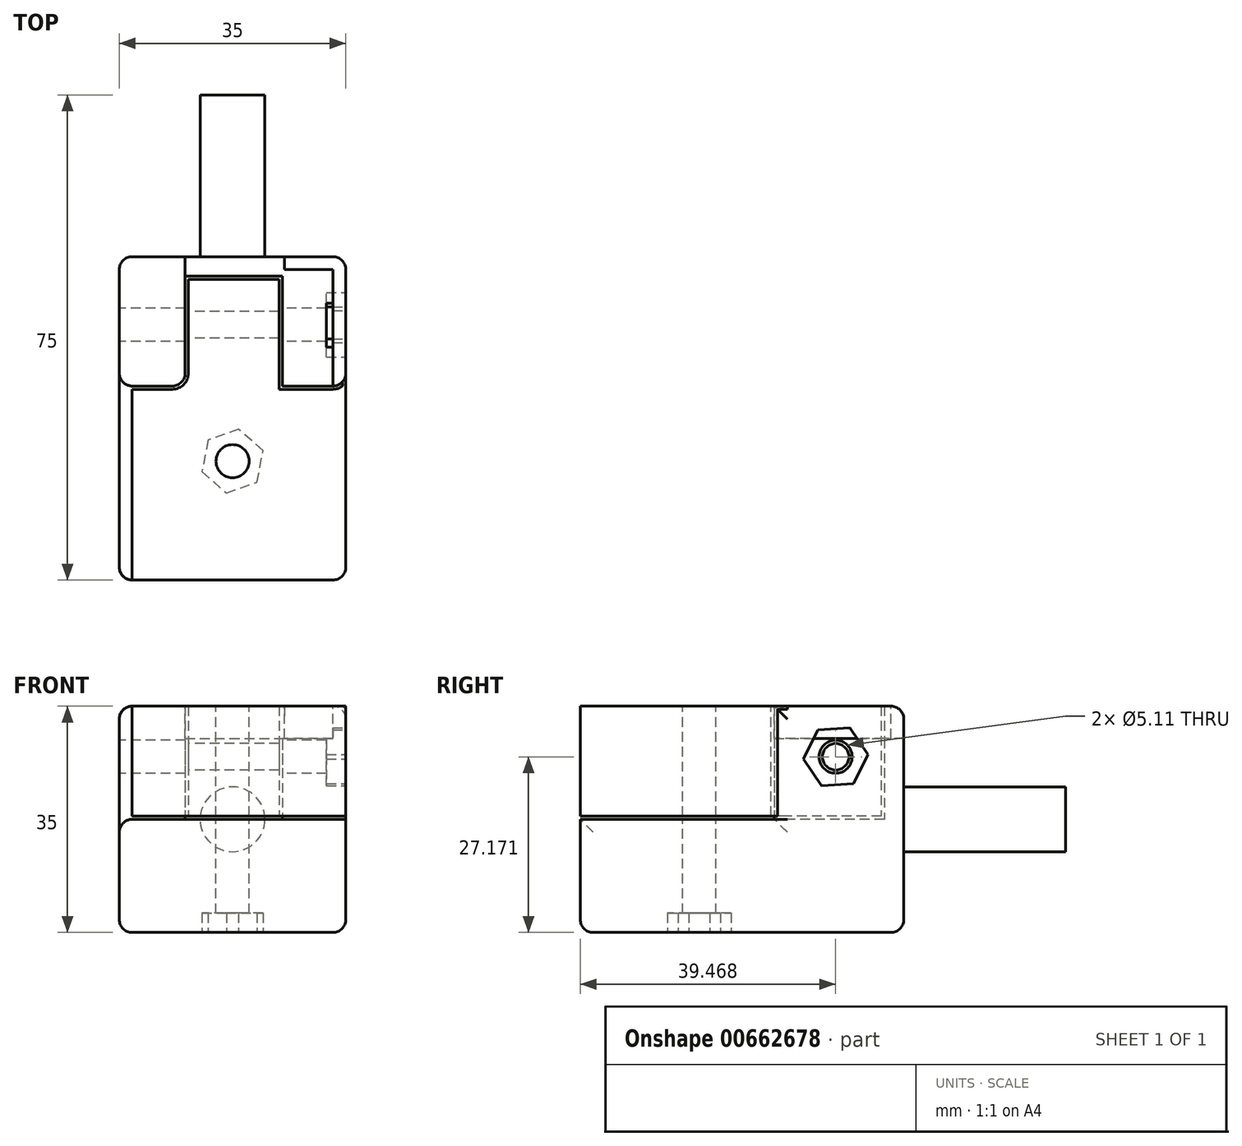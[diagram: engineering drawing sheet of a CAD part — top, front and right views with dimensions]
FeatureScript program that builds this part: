
annotation { "Feature Type Name" : "Feature", "Feature Type Description" : "" }
export const myFeature = defineFeature(function(context is Context, id is Id, definition is map)
    precondition{}
    {
        {
            var Q0;
            Q0=qCreatedBy(makeId("Front.planeOp"),FACE);
            var sketch = newSketch(context, id + "F0", { "sketchPlane" : qUnion([Q0])});
            skLineSegment(sketch, "E0.bottom", {"start": v(-17.5, -17.5) * mm, "end": v(17.5, -17.5) * mm});
            skLineSegment(sketch, "E0.top", {"start": v(-17.5, 17.5) * mm, "end": v(17.5, 17.5) * mm});
            skLineSegment(sketch, "E0.left", {"start": v(-17.5, -17.5) * mm, "end": v(-17.5, 17.5) * mm});
            skLineSegment(sketch, "E0.right", {"start": v(17.5, -17.5) * mm, "end": v(17.5, 17.5) * mm});
            skPoint(sketch, "E0.middle", {"position": v(0, 0) * mm});
            skSolve(sketch);
        }
        {
            var Q0;
            Q0=makeQuery(id+"F0.imprint","IMPRINT",FACE,{"disambiguationData":[TD([[makeQuery(id+"F0.imprint","IMPRINT",EDGE,{"derivedFrom":sQuery(id+"F0.wireOp",EDGE,"E0.bottom")}),1.0]])]});
            var Q1;
            Q1 = qSketchRegion(id + "F0", true);
            extrude(context, id + "F1", {"entities" : qUnion([Q0, Q1]), "depth" : 50 * mm, "offsetDistance" : 25 * mm});
        }
        {
            var Q0;
            Q0=makeQuery(id+"F1.opExtrude","SWEPT_FACE",FACE,{"disambiguationData":[OSD([sQuery(id+"F0.wireOp",EDGE,"E0.left")])]});
            var sketch = newSketch(context, id + "F2", { "sketchPlane" : qUnion([Q0])});
            skLineSegment(sketch, "E1.bottom", {"start": v(20, 17.5) * mm, "end": v(50, 17.5) * mm});
            skLineSegment(sketch, "E1.top", {"start": v(20, 0) * mm, "end": v(50, 0) * mm});
            skLineSegment(sketch, "E1.left", {"start": v(20, 17.5) * mm, "end": v(20, 0) * mm});
            skLineSegment(sketch, "E1.right", {"start": v(50, 17.5) * mm, "end": v(50, 0) * mm});
            skSolve(sketch);
        }
        {
            var Q0;
            Q0=makeQuery(id+"F2.imprint","IMPRINT",FACE,{"disambiguationData":[TD([[makeQuery(id+"F2.imprint","IMPRINT",EDGE,{"derivedFrom":sQuery(id+"F2.wireOp",EDGE,"E1.bottom")}),1.0]])]});
            extrude(context, id + "F3", {"entities" : qUnion([Q0]), "operationType" : NewBodyOperationType.REMOVE, "endBound" : BoundingType.THROUGH_ALL, "oppositeDirection" : true, "depth" : 25 * mm, "offsetDistance" : 25 * mm});
        }
        {
            var Q0;
            Q0=makeQuery(id+"F3.boolean.opBoolean","COPY",FACE,{"derivedFrom":makeQuery(id+"F3.opExtrude","SWEPT_FACE",FACE,{"disambiguationData":[OSD([sQuery(id+"F2.wireOp",EDGE,"E1.left")])]})});
            var sketch = newSketch(context, id + "F4", { "sketchPlane" : qUnion([Q0])});
            skLineSegment(sketch, "E2.bottom", {"start": v(-7.31, 17.5) * mm, "end": v(7.69, 17.5) * mm});
            skLineSegment(sketch, "E2.top", {"start": v(-7.31, 0) * mm, "end": v(7.69, 0) * mm});
            skLineSegment(sketch, "E2.left", {"start": v(-7.31, 17.5) * mm, "end": v(-7.31, 0) * mm});
            skLineSegment(sketch, "E2.right", {"start": v(7.69, 17.5) * mm, "end": v(7.69, 0) * mm});
            skSolve(sketch);
        }
        {
            var Q0;
            Q0=makeQuery(id+"F4.imprint","IMPRINT",FACE,{"disambiguationData":[TD([[makeQuery(id+"F4.imprint","IMPRINT",EDGE,{"derivedFrom":sQuery(id+"F4.wireOp",EDGE,"E2.bottom")}),1.0]])]});
            extrude(context, id + "F5", {"entities" : qUnion([Q0]), "operationType" : NewBodyOperationType.REMOVE, "oppositeDirection" : true, "depth" : 17 * mm, "offsetDistance" : 25 * mm});
        }
        {
            var Q0;
            Q0=makeQuery(id+"F1.opExtrude","SWEPT_EDGE",EDGE,{"disambiguationData":[OSD([sQuery(id+"F0.wireOp",EDGE,"E0.top"),sQuery(id+"F0.wireOp",EDGE,"E0.left")])]});
            var Q1;
            Q1=makeQuery(id+"F1.opExtrude","SWEPT_FACE",FACE,{"disambiguationData":[OSD([sQuery(id+"F0.wireOp",EDGE,"E0.left")])]});
            var Q2;
            Q2=makeQuery(id+"F1.opExtrude","CAP_EDGE",EDGE,{"disambiguationData":[OSD([sQuery(id+"F0.wireOp",EDGE,"E0.bottom")])],"isStart":false});
            var Q3;
            Q3=makeQuery(id+"F1.opExtrude","CAP_EDGE",EDGE,{"disambiguationData":[OSD([sQuery(id+"F0.wireOp",EDGE,"E0.right")])],"isStart":false});
            var Q4;
            Q4=makeQuery(id+"F1.opExtrude","SWEPT_EDGE",EDGE,{"disambiguationData":[OSD([sQuery(id+"F0.wireOp",EDGE,"E0.bottom"),sQuery(id+"F0.wireOp",EDGE,"E0.right")])]});
            var Q5;
            Q5=makeQuery(id+"F1.opExtrude","CAP_EDGE",EDGE,{"disambiguationData":[OSD([sQuery(id+"F0.wireOp",EDGE,"E0.right")])],"isStart":true});
            var Q6;
            Q6=makeQuery(id+"F1.opExtrude","SWEPT_EDGE",EDGE,{"disambiguationData":[OSD([sQuery(id+"F0.wireOp",EDGE,"E0.top"),sQuery(id+"F0.wireOp",EDGE,"E0.right")])]});
            var Q7;
            Q7=makeQuery(id+"F3.boolean.opBoolean","INTERSECT",EDGE,{"derivedFrom":[makeQuery(id+"F1.opExtrude","SWEPT_FACE",FACE,{"disambiguationData":[OSD([sQuery(id+"F0.wireOp",EDGE,"E0.right")])]}),makeQuery(id+"F3.opExtrude","SWEPT_FACE",FACE,{"disambiguationData":[OSD([sQuery(id+"F2.wireOp",EDGE,"E1.left")])]})]});
            var Q8;
            Q8=makeQuery(id+"F1.opExtrude","CAP_EDGE",EDGE,{"disambiguationData":[OSD([sQuery(id+"F0.wireOp",EDGE,"E0.top")])],"isStart":true});
            var Q9;
            Q9=makeQuery(id+"F1.opExtrude","CAP_EDGE",EDGE,{"disambiguationData":[OSD([sQuery(id+"F0.wireOp",EDGE,"E0.bottom")])],"isStart":true});
            var Q10;
            Q10=makeQuery(id+"F5.boolean.opBoolean","COPY",EDGE,{"derivedFrom":makeQuery(id+"F5.opExtrude","SWEPT_EDGE",EDGE,{"disambiguationData":[OSD([sQuery(id+"F0.wireOp",EDGE,"E0.top"),sQuery(id+"F0.wireOp",EDGE,"E0.left"),sQuery(id+"F2.wireOp",EDGE,"E1.bottom"),sQuery(id+"F2.wireOp",EDGE,"E1.left"),sQuery(id+"F4.wireOp",EDGE,"E2.bottom"),sQuery(id+"F4.wireOp",EDGE,"E2.left")])]})});
            var Q11;
            Q11=makeQuery(id+"F5.boolean.opBoolean","COPY",EDGE,{"derivedFrom":makeQuery(id+"F5.opExtrude","SWEPT_EDGE",EDGE,{"disambiguationData":[OSD([sQuery(id+"F0.wireOp",EDGE,"E0.top"),sQuery(id+"F0.wireOp",EDGE,"E0.left"),sQuery(id+"F2.wireOp",EDGE,"E1.bottom"),sQuery(id+"F2.wireOp",EDGE,"E1.left"),sQuery(id+"F4.wireOp",EDGE,"E2.bottom"),sQuery(id+"F4.wireOp",EDGE,"E2.right")])]})});
            var Q12;
            Q12=makeQuery(id+"F5.boolean.opBoolean","COPY",EDGE,{"derivedFrom":makeQuery(id+"F5.opExtrude","CAP_EDGE",EDGE,{"disambiguationData":[OSD([sQuery(id+"F4.wireOp",EDGE,"E2.left")])],"isStart":true})});
            var Q13;
            Q13=makeQuery(id+"F5.boolean.opBoolean","COPY",EDGE,{"derivedFrom":makeQuery(id+"F5.opExtrude","CAP_EDGE",EDGE,{"disambiguationData":[OSD([sQuery(id+"F4.wireOp",EDGE,"E2.right")])],"isStart":true})});
            var Q14;
            {var subQ0=sQuery(id+"F0.wireOp",EDGE,"E0.top");var subQ1=sQuery(id+"F0.wireOp",EDGE,"E0.left");var subQ2=sQuery(id+"F2.wireOp",EDGE,"E1.left");Q14=makeQuery(id+"F5.boolean.opBoolean","SPLIT",EDGE,{"disambiguationData":[TD([makeQuery(id+"F1.opExtrude","SWEPT_FACE",FACE,{"disambiguationData":[OSD([subQ1])]})])],"derivedFrom":makeQuery(id+"F3.boolean.opBoolean","COPY",EDGE,{"derivedFrom":makeQuery(id+"F3.opExtrude","SWEPT_EDGE",EDGE,{"disambiguationData":[OSD([subQ0,subQ1,sQuery(id+"F2.wireOp",EDGE,"E1.bottom"),subQ2])]})})});}
            var Q15;
            {var subQ0=sQuery(id+"F0.wireOp",EDGE,"E0.top");var subQ1=sQuery(id+"F2.wireOp",EDGE,"E1.left");Q15=makeQuery(id+"F5.boolean.opBoolean","SPLIT",EDGE,{"disambiguationData":[TD([makeQuery(id+"F1.opExtrude","SWEPT_FACE",FACE,{"disambiguationData":[OSD([sQuery(id+"F0.wireOp",EDGE,"E0.right")])]})])],"derivedFrom":makeQuery(id+"F3.boolean.opBoolean","COPY",EDGE,{"derivedFrom":makeQuery(id+"F3.opExtrude","SWEPT_EDGE",EDGE,{"disambiguationData":[OSD([subQ0,sQuery(id+"F0.wireOp",EDGE,"E0.left"),sQuery(id+"F2.wireOp",EDGE,"E1.bottom"),subQ1])]})})});}
            fillet(context, id + "F6", {"entities" : qUnion([Q0, Q1, Q2, Q3, Q4, Q5, Q6, Q7, Q8, Q9, Q10, Q11, Q12, Q13, Q14, Q15]), "radius" : 2 * mm, "tangentPropagation" : true, "allowEdgeOverflow" : false});
        }
        {
            var Q0;
            Q0=makeQuery(id+"F1.opExtrude","CAP_FACE",FACE,{"disambiguationData":[OSD([sQuery(id+"F0.wireOp",EDGE,"E0.bottom"),sQuery(id+"F0.wireOp",EDGE,"E0.top"),sQuery(id+"F0.wireOp",EDGE,"E0.left"),sQuery(id+"F0.wireOp",EDGE,"E0.right")])],"isStart":true});
            var sketch = newSketch(context, id + "F7", { "sketchPlane" : qUnion([Q0])});
            skCircle(sketch, "E3", {"center": v(0, 0) * mm, "radius": 5 * mm});
            skSolve(sketch);
        }
        {
            var Q0;
            Q0=makeQuery(id+"F7.imprint","IMPRINT",FACE,{"disambiguationData":[TD([[makeQuery(id+"F7.imprint","IMPRINT",EDGE,{"derivedFrom":sQuery(id+"F7.wireOp",EDGE,"E3")}),1.0]])]});
            extrude(context, id + "F8", {"entities" : qUnion([Q0]), "operationType" : NewBodyOperationType.ADD, "depth" : 25 * mm, "offsetDistance" : 25 * mm});
        }
        {
            var Q0;
            Q0=makeQuery(id+"F1.opExtrude","SWEPT_FACE",FACE,{"disambiguationData":[OSD([sQuery(id+"F0.wireOp",EDGE,"E0.left")])]});
            var sketch = newSketch(context, id + "F9", { "sketchPlane" : qUnion([Q0])});
            skPoint(sketch, "E4", {"position": v(10.53, 9.67) * mm});
            skSolve(sketch);
        }
        {
            var Q0;
            Q0=sQuery(id+"F9.wireOp",VERTEX,"E4");
            var Q1;
            Q1=makeQuery(id+"F1.opExtrude","SWEPT_BODY",BODY,{"disambiguationData":[OSD([sQuery(id+"F0.wireOp",EDGE,"E0.bottom"),sQuery(id+"F0.wireOp",EDGE,"E0.top"),sQuery(id+"F0.wireOp",EDGE,"E0.left"),sQuery(id+"F0.wireOp",EDGE,"E0.right")])]});
            hole(context, id + "F10", {"style" : HoleStyle.SIMPLE, "endStyle" : HoleEndStyle.BLIND, "standardTappedOrClearance" : lookupTablePath({ "standard" : "ANSI", "fit" : "Normal (ASME)", "size" : "#10", "type" : "Clearance" }), "standardBlindInLast" : lookupTablePath({ "fit" : "Free", "standard" : "ANSI", "size" : "#10", "type" : "Clearance" }), "holeDiameter" : 5.1 * mm, "majorDiameter" : 5 * mm, "holeDepth" : 60 * mm, "isTappedThrough" : true, "tappedDepth" : 12.7 * mm, "tapClearance" : 3, "locations" : qUnion([Q0]), "scope" : qUnion([Q1])});
        }
        {
            var Q0;
            Q0=makeQuery(id+"F5.boolean.opBoolean","MERGE",FACE,{"derivedFrom":[makeQuery(id+"F3.boolean.opBoolean","COPY",FACE,{"derivedFrom":makeQuery(id+"F3.opExtrude","SWEPT_FACE",FACE,{"disambiguationData":[OSD([sQuery(id+"F2.wireOp",EDGE,"E1.top")])]})}),makeQuery(id+"F5.opExtrude","SWEPT_FACE",FACE,{"disambiguationData":[OSD([sQuery(id+"F4.wireOp",EDGE,"E2.top")])]})]});
            var sketch = newSketch(context, id + "F11", { "sketchPlane" : qUnion([Q0])});
            skLineSegment(sketch, "E5.0", {"start": v(15.5, -50) * mm, "end": v(-15.5, -50) * mm});
            skLineSegment(sketch, "E6.0.0", {"start": v(-9.31, -20) * mm, "end": v(-15.5, -20) * mm});
            skLineSegment(sketch, "E6.0.1", {"start": v(-15.5, -20) * mm, "end": v(-15.5, -50) * mm});
            skLineSegment(sketch, "E6.0.2", {"start": v(-15.5, -50) * mm, "end": v(15.5, -50) * mm});
            skArc(sketch, "E6.0.3", {"start": v(15.5, -50) * mm, "mid": v(16.91, -49.41) * mm, "end": v(17.5, -48) * mm});
            skLineSegment(sketch, "E6.0.4", {"start": v(17.5, -48) * mm, "end": v(17.5, -18) * mm});
            skArc(sketch, "E6.0.5", {"start": v(17.5, -18) * mm, "mid": v(16.91, -19.41) * mm, "end": v(15.5, -20) * mm});
            skLineSegment(sketch, "E6.0.6", {"start": v(15.5, -20) * mm, "end": v(9.69, -20) * mm});
            skArc(sketch, "E6.0.7", {"start": v(9.69, -20) * mm, "mid": v(8.27, -19.41) * mm, "end": v(7.69, -18) * mm});
            skLineSegment(sketch, "E6.0.8", {"start": v(7.69, -18) * mm, "end": v(7.69, -3) * mm});
            skLineSegment(sketch, "E6.0.9", {"start": v(7.69, -3) * mm, "end": v(-7.31, -3) * mm});
            skLineSegment(sketch, "E6.0.10", {"start": v(-7.31, -3) * mm, "end": v(-7.31, -18) * mm});
            skArc(sketch, "E6.0.11", {"start": v(-7.31, -18) * mm, "mid": v(-7.9, -19.41) * mm, "end": v(-9.31, -20) * mm});
            skSolve(sketch);
        }
        {
            var Q0;
            Q0 = qSketchRegion(id + "F11", true);
            var Q1;
            Q1=makeQuery(id+"F1.opExtrude","SWEPT_FACE",FACE,{"disambiguationData":[OSD([sQuery(id+"F0.wireOp",EDGE,"E0.top")])]});
            extrude(context, id + "F12", {"entities" : qUnion([Q0]), "endBound" : BoundingType.UP_TO_SURFACE, "depth" : 25 * mm, "endBoundEntityFace" : qUnion([Q1]), "offsetDistance" : 25 * mm});
        }
        {
            var Q0;
            Q0=makeQuery(id+"F1.opExtrude","SWEPT_BODY",BODY,{"disambiguationData":[OSD([sQuery(id+"F0.wireOp",EDGE,"E0.bottom"),sQuery(id+"F0.wireOp",EDGE,"E0.top"),sQuery(id+"F0.wireOp",EDGE,"E0.left"),sQuery(id+"F0.wireOp",EDGE,"E0.right")])]});
            var Q1;
            Q1=makeQuery(id+"F12.opExtrude","SWEPT_BODY",BODY,{"disambiguationData":[OSD([sQuery(id+"F11.wireOp",EDGE,"E6.0.0"),sQuery(id+"F11.wireOp",EDGE,"E6.0.1"),sQuery(id+"F11.wireOp",EDGE,"E6.0.2"),sQuery(id+"F11.wireOp",EDGE,"E6.0.3"),sQuery(id+"F11.wireOp",EDGE,"E6.0.4"),sQuery(id+"F11.wireOp",EDGE,"E6.0.5"),sQuery(id+"F11.wireOp",EDGE,"E6.0.6"),sQuery(id+"F11.wireOp",EDGE,"E6.0.7"),sQuery(id+"F11.wireOp",EDGE,"E6.0.8"),sQuery(id+"F11.wireOp",EDGE,"E6.0.9"),sQuery(id+"F11.wireOp",EDGE,"E6.0.10"),sQuery(id+"F11.wireOp",EDGE,"E6.0.11")])]});
            booleanBodies(context, id + "F13", {"operationType" : BooleanOperationType.SUBTRACTION, "tools" : qUnion([Q0]), "targets" : qUnion([Q1]), "offset" : true, "offsetAll" : true, "offsetDistance" : .5 * mm, "keepTools" : true});
        }
        {
            var Q0;
            Q0=makeQuery(id+"F13.tempBoolean.opBoolean","SPLIT",FACE,{"disambiguationData":[TD([makeQuery(id+"F13.offsetTempBody.opPattern","COPY",FACE,{"derivedFrom":makeQuery(id+"F10.hole-0.boolean.opBoolean","COPY",FACE,{"disambiguationData":[TD([makeQuery(id+"F1.opExtrude","SWEPT_FACE",FACE,{"disambiguationData":[OSD([sQuery(id+"F0.wireOp",EDGE,"E0.left")])]})])],"derivedFrom":makeQuery(id+"F10.hole-0.opRevolve","SWEPT_FACE",FACE,{"disambiguationData":[OSD([sQuery(id+"F10.hole-0.sketch.wireOp",EDGE,"core_line_2")])]})}),"instanceName":"1"})])],"derivedFrom":makeQuery(id+"F12.opExtrude","SWEPT_FACE",FACE,{"disambiguationData":[OSD([sQuery(id+"F11.wireOp",EDGE,"E6.0.10")])]})});
            extrude(context, id + "F14", {"entities" : qUnion([Q0]), "operationType" : NewBodyOperationType.REMOVE, "endBound" : BoundingType.THROUGH_ALL, "oppositeDirection" : true, "depth" : 25 * mm, "offsetDistance" : 25 * mm});
        }
        {
            var Q0;
            Q0=makeQuery(id+"F1.opExtrude","SWEPT_FACE",FACE,{"disambiguationData":[OSD([sQuery(id+"F0.wireOp",EDGE,"E0.top")])]});
            var sketch = newSketch(context, id + "F15", { "sketchPlane" : qUnion([Q0])});
            skLineSegment(sketch, "E7.bottom", {"start": v(-7.36, 0) * mm, "end": v(8.03, 0) * mm});
            skLineSegment(sketch, "E7.top", {"start": v(-7.36, -3) * mm, "end": v(8.03, -3) * mm});
            skLineSegment(sketch, "E7.left", {"start": v(-7.36, 0) * mm, "end": v(-7.36, -3) * mm});
            skLineSegment(sketch, "E7.right", {"start": v(8.03, 0) * mm, "end": v(8.03, -3) * mm});
            skSolve(sketch);
        }
        {
            var Q0;
            {var subQ0=sQuery(id+"F15.wireOp",EDGE,"E7.bottom");Q0=makeQuery(id+"F15.imprint","IMPRINT",FACE,{"disambiguationData":[TD([[makeQuery(id+"F15.imprint","IMPRINT",EDGE,{"derivedFrom":subQ0}),-1.0]])]});}
            var Q1;
            {var subQ0=sQuery(id+"F15.wireOp",EDGE,"E7.top");Q1=makeQuery(id+"F15.imprint","IMPRINT",FACE,{"disambiguationData":[TD([[makeQuery(id+"F15.imprint","IMPRINT",EDGE,{"derivedFrom":subQ0}),-1.0]])]});}
            extrude(context, id + "F16", {"entities" : qUnion([Q0, Q1]), "operationType" : NewBodyOperationType.REMOVE, "oppositeDirection" : true, "depth" : 5 * mm, "offsetDistance" : 25 * mm});
        }
        {
            var Q0;
            Q0=makeQuery(id+"F12.opExtrude","CAP_FACE",FACE,{"disambiguationData":[OSD([sQuery(id+"F11.wireOp",EDGE,"E6.0.0"),sQuery(id+"F11.wireOp",EDGE,"E6.0.1"),sQuery(id+"F11.wireOp",EDGE,"E6.0.2"),sQuery(id+"F11.wireOp",EDGE,"E6.0.3"),sQuery(id+"F11.wireOp",EDGE,"E6.0.4"),sQuery(id+"F11.wireOp",EDGE,"E6.0.5"),sQuery(id+"F11.wireOp",EDGE,"E6.0.6"),sQuery(id+"F11.wireOp",EDGE,"E6.0.7"),sQuery(id+"F11.wireOp",EDGE,"E6.0.8"),sQuery(id+"F11.wireOp",EDGE,"E6.0.9"),sQuery(id+"F11.wireOp",EDGE,"E6.0.10"),sQuery(id+"F11.wireOp",EDGE,"E6.0.11")])],"isStart":false});
            var sketch = newSketch(context, id + "F17", { "sketchPlane" : qUnion([Q0])});
            skPoint(sketch, "E8", {"position": v(0, -31.61) * mm});
            skSolve(sketch);
        }
        {
            var Q0;
            Q0=sQuery(id+"F17.wireOp",VERTEX,"E8");
            var Q1;
            Q1=makeQuery(id+"F1.opExtrude","SWEPT_BODY",BODY,{"disambiguationData":[OSD([sQuery(id+"F0.wireOp",EDGE,"E0.bottom"),sQuery(id+"F0.wireOp",EDGE,"E0.top"),sQuery(id+"F0.wireOp",EDGE,"E0.left"),sQuery(id+"F0.wireOp",EDGE,"E0.right")])]});
            var Q2;
            Q2=makeQuery(id+"F12.opExtrude","SWEPT_BODY",BODY,{"disambiguationData":[OSD([sQuery(id+"F11.wireOp",EDGE,"E6.0.0"),sQuery(id+"F11.wireOp",EDGE,"E6.0.1"),sQuery(id+"F11.wireOp",EDGE,"E6.0.2"),sQuery(id+"F11.wireOp",EDGE,"E6.0.3"),sQuery(id+"F11.wireOp",EDGE,"E6.0.4"),sQuery(id+"F11.wireOp",EDGE,"E6.0.5"),sQuery(id+"F11.wireOp",EDGE,"E6.0.6"),sQuery(id+"F11.wireOp",EDGE,"E6.0.7"),sQuery(id+"F11.wireOp",EDGE,"E6.0.8"),sQuery(id+"F11.wireOp",EDGE,"E6.0.9"),sQuery(id+"F11.wireOp",EDGE,"E6.0.10"),sQuery(id+"F11.wireOp",EDGE,"E6.0.11")])]});
            hole(context, id + "F18", {"style" : HoleStyle.SIMPLE, "endStyle" : HoleEndStyle.THROUGH, "standardTappedOrClearance" : lookupTablePath({ "standard" : "ANSI", "fit" : "Normal (ASME)", "size" : "#10", "type" : "Clearance" }), "standardBlindInLast" : lookupTablePath({ "fit" : "Free", "standard" : "ANSI", "size" : "#10", "type" : "Clearance" }), "holeDiameter" : 5.1 * mm, "majorDiameter" : 4.83 * mm, "isTappedThrough" : true, "tappedDepth" : 12.7 * mm, "tapClearance" : 3, "locations" : qUnion([Q0]), "scope" : qUnion([Q1, Q2])});
        }
        {
            var Q0;
            Q0=makeQuery(id+"F1.opExtrude","SWEPT_FACE",FACE,{"disambiguationData":[OSD([sQuery(id+"F0.wireOp",EDGE,"E0.bottom")])]});
            var sketch = newSketch(context, id + "F19", { "sketchPlane" : qUnion([Q0])});
            skCircle(sketch, "E9.cCircle", {"center": v(0, 31.61) * mm, "radius": 4.33 * mm, "construction": true});
            skLineSegment(sketch, "E9.0", {"start": v(4.72, 29.98) * mm, "end": v(0.94, 26.7) * mm});
            skLineSegment(sketch, "E9.1", {"start": v(0.94, 26.7) * mm, "end": v(-3.78, 28.34) * mm});
            skLineSegment(sketch, "E9.2", {"start": v(-3.78, 28.34) * mm, "end": v(-4.72, 33.25) * mm});
            skLineSegment(sketch, "E9.3", {"start": v(-4.72, 33.25) * mm, "end": v(-0.94, 36.52) * mm});
            skLineSegment(sketch, "E9.4", {"start": v(-0.94, 36.52) * mm, "end": v(3.78, 34.89) * mm});
            skLineSegment(sketch, "E9.5", {"start": v(3.78, 34.89) * mm, "end": v(4.72, 29.98) * mm});
            skPoint(sketch, "E9.0.midPoint", {"position": v(2.83, 28.34) * mm});
            skSolve(sketch);
        }
        {
            var Q0;
            Q0=makeQuery(id+"F19.imprint","IMPRINT",FACE,{"disambiguationData":[TD([[makeQuery(id+"F19.imprint","IMPRINT",EDGE,{"derivedFrom":sQuery(id+"F19.wireOp",EDGE,"E9.0")}),-1.0]])]});
            extrude(context, id + "F20", {"entities" : qUnion([Q0]), "operationType" : NewBodyOperationType.REMOVE, "oppositeDirection" : true, "depth" : 3 * mm, "offsetDistance" : 25 * mm});
        }
        {
            var Q0;
            Q0=makeQuery(id+"F1.opExtrude","SWEPT_FACE",FACE,{"disambiguationData":[OSD([sQuery(id+"F0.wireOp",EDGE,"E0.right")])]});
            var sketch = newSketch(context, id + "F21", { "sketchPlane" : qUnion([Q0])});
            skCircle(sketch, "E10.cCircle", {"center": v(-10.53, 9.67) * mm, "radius": 4.33 * mm, "construction": true});
            skPoint(sketch, "E10.cCircle.perimeterSnap0", {"position": v(-18, 7.75) * mm});
            skLineSegment(sketch, "E10.0", {"start": v(-5.54, 10) * mm, "end": v(-7.76, 5.5) * mm});
            skLineSegment(sketch, "E10.1", {"start": v(-7.76, 5.5) * mm, "end": v(-12.75, 5.19) * mm});
            skLineSegment(sketch, "E10.2", {"start": v(-12.75, 5.19) * mm, "end": v(-15.52, 9.35) * mm});
            skLineSegment(sketch, "E10.3", {"start": v(-15.52, 9.35) * mm, "end": v(-13.3, 13.83) * mm});
            skLineSegment(sketch, "E10.4", {"start": v(-13.3, 13.83) * mm, "end": v(-8.31, 14.15) * mm});
            skLineSegment(sketch, "E10.5", {"start": v(-8.31, 14.15) * mm, "end": v(-5.54, 10) * mm});
            skPoint(sketch, "E10.0.midPoint", {"position": v(-6.65, 7.75) * mm});
            skPoint(sketch, "E10.0.midPoint.positionSnap0", {"position": v(-18, 7.75) * mm});
            skSolve(sketch);
        }
        {
            var Q0;
            Q0=makeQuery(id+"F21.imprint","IMPRINT",FACE,{"disambiguationData":[TD([[makeQuery(id+"F21.imprint","IMPRINT",EDGE,{"derivedFrom":sQuery(id+"F21.wireOp",EDGE,"E10.0")}),-1.0]])]});
            extrude(context, id + "F22", {"entities" : qUnion([Q0]), "operationType" : NewBodyOperationType.REMOVE, "oppositeDirection" : true, "depth" : 3 * mm, "offsetDistance" : 25 * mm});
        }
    });
